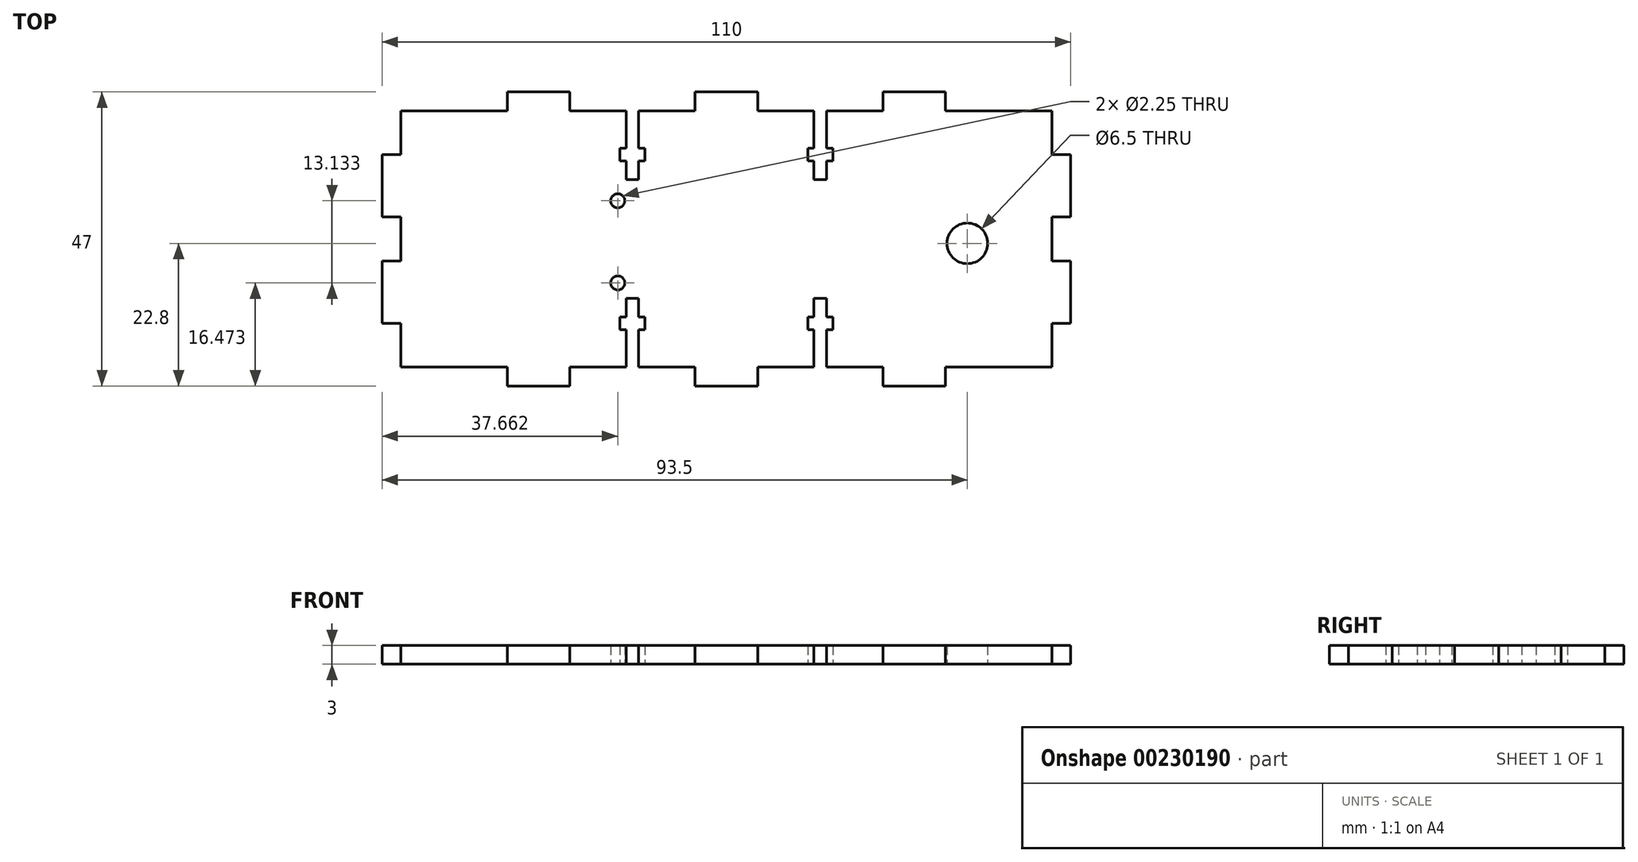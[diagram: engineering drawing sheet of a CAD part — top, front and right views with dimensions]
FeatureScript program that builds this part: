
annotation { "Feature Type Name" : "Feature", "Feature Type Description" : "" }
export const myFeature = defineFeature(function(context is Context, id is Id, definition is map)
    precondition{}
    {
        {
            var Q0;
            Q0=qCreatedBy(makeId("Top.planeOp"),FACE);
            var sketch = newSketch(context, id + "F0", { "sketchPlane" : qUnion([Q0])});
            skLineSegment(sketch, "E0", {"start": v(0, 0) * mm, "end": v(0, 7) * mm});
            skLineSegment(sketch, "E1", {"start": v(0, 7) * mm, "end": v(3, 7) * mm});
            skLineSegment(sketch, "E2", {"start": v(3, 7) * mm, "end": v(3, 17) * mm});
            skLineSegment(sketch, "E3", {"start": v(3, 17) * mm, "end": v(0, 17) * mm});
            skLineSegment(sketch, "E4", {"start": v(0, 17) * mm, "end": v(0, 24) * mm});
            skLineSegment(sketch, "E5", {"start": v(0, 24) * mm, "end": v(3, 24) * mm});
            skLineSegment(sketch, "E6", {"start": v(3, 24) * mm, "end": v(3, 34) * mm});
            skLineSegment(sketch, "E7", {"start": v(3, 34) * mm, "end": v(0, 34) * mm});
            skLineSegment(sketch, "E8", {"start": v(0, 34) * mm, "end": v(0, 41) * mm});
            skLineSegment(sketch, "E9", {"start": v(0, 41) * mm, "end": v(-17, 41) * mm});
            skLineSegment(sketch, "E10", {"start": v(-17, 41) * mm, "end": v(-17, 44) * mm});
            skLineSegment(sketch, "E11", {"start": v(-17, 44) * mm, "end": v(-27, 44) * mm});
            skLineSegment(sketch, "E12", {"start": v(-27, 44) * mm, "end": v(-27, 41) * mm});
            skLineSegment(sketch, "E13", {"start": v(-47, 41) * mm, "end": v(-47, 44) * mm});
            skLineSegment(sketch, "E14", {"start": v(-47, -3) * mm, "end": v(-47, 0) * mm});
            skLineSegment(sketch, "E15", {"start": v(-47, 0) * mm, "end": v(-38, 0) * mm});
            skLineSegment(sketch, "E16", {"start": v(-27, 0) * mm, "end": v(-27, -3) * mm});
            skLineSegment(sketch, "E17", {"start": v(-27, -3) * mm, "end": v(-17, -3) * mm});
            skLineSegment(sketch, "E18", {"start": v(-17, 0) * mm, "end": v(-17, -3) * mm});
            skLineSegment(sketch, "E19", {"start": v(-17, 0) * mm, "end": v(0, 0) * mm});
            skLineSegment(sketch, "E20", {"start": v(-47, 41) * mm, "end": v(-38, 41) * mm});
            skLineSegment(sketch, "E21", {"start": v(-27, 41) * mm, "end": v(-36, 41) * mm});
            skLineSegment(sketch, "E22", {"start": v(-38, 41) * mm, "end": v(-38, 35) * mm});
            skLineSegment(sketch, "E23", {"start": v(-38, 35) * mm, "end": v(-39, 35) * mm});
            skLineSegment(sketch, "E24", {"start": v(-39, 35) * mm, "end": v(-39, 33) * mm});
            skLineSegment(sketch, "E25", {"start": v(-39, 33) * mm, "end": v(-38, 33) * mm});
            skLineSegment(sketch, "E26", {"start": v(-38, 33) * mm, "end": v(-38, 30) * mm});
            skLineSegment(sketch, "E27", {"start": v(-38, 30) * mm, "end": v(-36, 30) * mm});
            skLineSegment(sketch, "E28", {"start": v(-36, 30) * mm, "end": v(-36, 33) * mm});
            skLineSegment(sketch, "E29", {"start": v(-36, 33) * mm, "end": v(-35, 33) * mm});
            skLineSegment(sketch, "E30", {"start": v(-35, 33) * mm, "end": v(-35, 35) * mm});
            skLineSegment(sketch, "E31", {"start": v(-35, 35) * mm, "end": v(-36, 35) * mm});
            skLineSegment(sketch, "E32", {"start": v(-36, 35) * mm, "end": v(-36, 41) * mm});
            skLineSegment(sketch, "E33.MirrorCS", {"start": v(-39, 8) * mm, "end": v(-38, 8) * mm});
            skLineSegment(sketch, "E34.MirrorCS", {"start": v(-36, 8) * mm, "end": v(-35, 8) * mm});
            skLineSegment(sketch, "E35.MirrorCS", {"start": v(-35, 6) * mm, "end": v(-36, 6) * mm});
            skLineSegment(sketch, "E36.MirrorCS", {"start": v(-38, 6) * mm, "end": v(-39, 6) * mm});
            skLineSegment(sketch, "E37.MirrorCS", {"start": v(-38, 11) * mm, "end": v(-36, 11) * mm});
            skLineSegment(sketch, "E38.MirrorCS", {"start": v(-38, 8) * mm, "end": v(-38, 11) * mm});
            skLineSegment(sketch, "E39.MirrorCS", {"start": v(-36, 11) * mm, "end": v(-36, 8) * mm});
            skLineSegment(sketch, "E40.MirrorCS", {"start": v(-35, 8) * mm, "end": v(-35, 6) * mm});
            skLineSegment(sketch, "E41.MirrorCS", {"start": v(-39, 6) * mm, "end": v(-39, 8) * mm});
            skLineSegment(sketch, "E42.MirrorCS", {"start": v(-38, 0) * mm, "end": v(-38, 6) * mm});
            skLineSegment(sketch, "E43.MirrorCS", {"start": v(-36, 6) * mm, "end": v(-36, 0) * mm});
            skLineSegment(sketch, "E44.trimOffspring", {"start": v(-36, 0) * mm, "end": v(-27, 0) * mm});
            skLineSegment(sketch, "E45.MirrorCS", {"start": v(-69, 33) * mm, "end": v(-69, 35) * mm});
            skLineSegment(sketch, "E46.MirrorCS", {"start": v(-69, 35) * mm, "end": v(-68, 35) * mm});
            skLineSegment(sketch, "E47.MirrorCS", {"start": v(-65, 35) * mm, "end": v(-65, 33) * mm});
            skLineSegment(sketch, "E48.MirrorCS", {"start": v(-68, 8) * mm, "end": v(-69, 8) * mm});
            skLineSegment(sketch, "E49.MirrorCS", {"start": v(-65, 33) * mm, "end": v(-66, 33) * mm});
            skLineSegment(sketch, "E50.MirrorCS", {"start": v(-68, 33) * mm, "end": v(-69, 33) * mm});
            skLineSegment(sketch, "E51.MirrorCS", {"start": v(-65, 8) * mm, "end": v(-66, 8) * mm});
            skLineSegment(sketch, "E52.MirrorCS", {"start": v(-65, 6) * mm, "end": v(-65, 8) * mm});
            skLineSegment(sketch, "E53.MirrorCS", {"start": v(-69, 8) * mm, "end": v(-69, 6) * mm});
            skLineSegment(sketch, "E54.MirrorCS", {"start": v(-69, 6) * mm, "end": v(-68, 6) * mm});
            skLineSegment(sketch, "E55.MirrorCS", {"start": v(-87, 0) * mm, "end": v(-87, -3) * mm});
            skLineSegment(sketch, "E56.MirrorCS", {"start": v(-66, 30) * mm, "end": v(-68, 30) * mm});
            skLineSegment(sketch, "E57.MirrorCS", {"start": v(-77, 44) * mm, "end": v(-77, 41) * mm});
            skLineSegment(sketch, "E58.MirrorCS", {"start": v(-66, 33) * mm, "end": v(-66, 30) * mm});
            skLineSegment(sketch, "E59.MirrorCS", {"start": v(-66, 8) * mm, "end": v(-66, 11) * mm});
            skLineSegment(sketch, "E60.MirrorCS", {"start": v(-68, 11) * mm, "end": v(-68, 8) * mm});
            skLineSegment(sketch, "E61.MirrorCS", {"start": v(-66, 6) * mm, "end": v(-65, 6) * mm});
            skLineSegment(sketch, "E62.MirrorCS", {"start": v(-104, 24) * mm, "end": v(-107, 24) * mm});
            skLineSegment(sketch, "E63.MirrorCS", {"start": v(-77, 0) * mm, "end": v(-77, -3) * mm});
            skLineSegment(sketch, "E64.MirrorCS", {"start": v(-57, 41) * mm, "end": v(-57, 44) * mm});
            skLineSegment(sketch, "E65.MirrorCS", {"start": v(-66, 35) * mm, "end": v(-65, 35) * mm});
            skLineSegment(sketch, "E66.MirrorCS", {"start": v(-68, 30) * mm, "end": v(-68, 33) * mm});
            skLineSegment(sketch, "E67.MirrorCS", {"start": v(-87, 41) * mm, "end": v(-87, 44) * mm});
            skLineSegment(sketch, "E68.MirrorCS", {"start": v(-66, 11) * mm, "end": v(-68, 11) * mm});
            skLineSegment(sketch, "E69.MirrorCS", {"start": v(-104, 7) * mm, "end": v(-107, 7) * mm});
            skLineSegment(sketch, "E70.MirrorCS", {"start": v(-107, 34) * mm, "end": v(-104, 34) * mm});
            skLineSegment(sketch, "E71.MirrorCS", {"start": v(-107, 17) * mm, "end": v(-104, 17) * mm});
            skLineSegment(sketch, "E72.MirrorCS", {"start": v(-57, -3) * mm, "end": v(-57, 0) * mm});
            skLineSegment(sketch, "E73.MirrorCS", {"start": v(-68, 35) * mm, "end": v(-68, 41) * mm});
            skLineSegment(sketch, "E74.MirrorCS", {"start": v(-104, 17) * mm, "end": v(-104, 24) * mm});
            skLineSegment(sketch, "E75.MirrorCS", {"start": v(-87, 0) * mm, "end": v(-104, 0) * mm});
            skLineSegment(sketch, "E76.MirrorCS", {"start": v(-104, 41) * mm, "end": v(-87, 41) * mm});
            skLineSegment(sketch, "E77.MirrorCS", {"start": v(-104, 0) * mm, "end": v(-104, 7) * mm});
            skLineSegment(sketch, "E78.MirrorCS", {"start": v(-68, 0) * mm, "end": v(-77, 0) * mm});
            skLineSegment(sketch, "E79.MirrorCS", {"start": v(-87, 44) * mm, "end": v(-77, 44) * mm});
            skLineSegment(sketch, "E80.MirrorCS", {"start": v(-66, 0) * mm, "end": v(-66, 6) * mm});
            skLineSegment(sketch, "E81.MirrorCS", {"start": v(-77, 41) * mm, "end": v(-68, 41) * mm});
            skLineSegment(sketch, "E82.MirrorCS", {"start": v(-68, 6) * mm, "end": v(-68, 0) * mm});
            skLineSegment(sketch, "E83.MirrorCS", {"start": v(-104, 34) * mm, "end": v(-104, 41) * mm});
            skLineSegment(sketch, "E84.MirrorCS", {"start": v(-66, 41) * mm, "end": v(-66, 35) * mm});
            skLineSegment(sketch, "E85.MirrorCS", {"start": v(-107, 24) * mm, "end": v(-107, 34) * mm});
            skLineSegment(sketch, "E86.MirrorCS", {"start": v(-77, -3) * mm, "end": v(-87, -3) * mm});
            skLineSegment(sketch, "E87.MirrorCS", {"start": v(-107, 7) * mm, "end": v(-107, 17) * mm});
            skLineSegment(sketch, "E88.MirrorCS", {"start": v(-57, 41) * mm, "end": v(-66, 41) * mm});
            skLineSegment(sketch, "E89.MirrorCS", {"start": v(-57, 0) * mm, "end": v(-66, 0) * mm});
            skCircle(sketch, "E90", {"center": v(-13.5, 19.8) * mm, "radius": 3.25 * mm});
            skCircle(sketch, "E91", {"center": v(-69.34, 26.6) * mm, "radius": 1.13 * mm});
            skCircle(sketch, "E92", {"center": v(-69.34, 13.47) * mm, "radius": 1.13 * mm});
            skLineSegment(sketch, "E93", {"start": v(-57, 44) * mm, "end": v(-47, 44) * mm});
            skLineSegment(sketch, "E94", {"start": v(-57, -3) * mm, "end": v(-47, -3) * mm});
            skSolve(sketch);
        }
        {
            var Q0;
            Q0=makeQuery(id+"F0.imprint","IMPRINT",FACE,{"disambiguationData":[TD([[makeQuery(id+"F0.imprint","IMPRINT",EDGE,{"derivedFrom":sQuery(id+"F0.wireOp",EDGE,"E0")}),1.0]])]});
            extrude(context, id + "F1", {"entities" : qUnion([Q0]), "depth" : 3 * mm});
        }
    });
